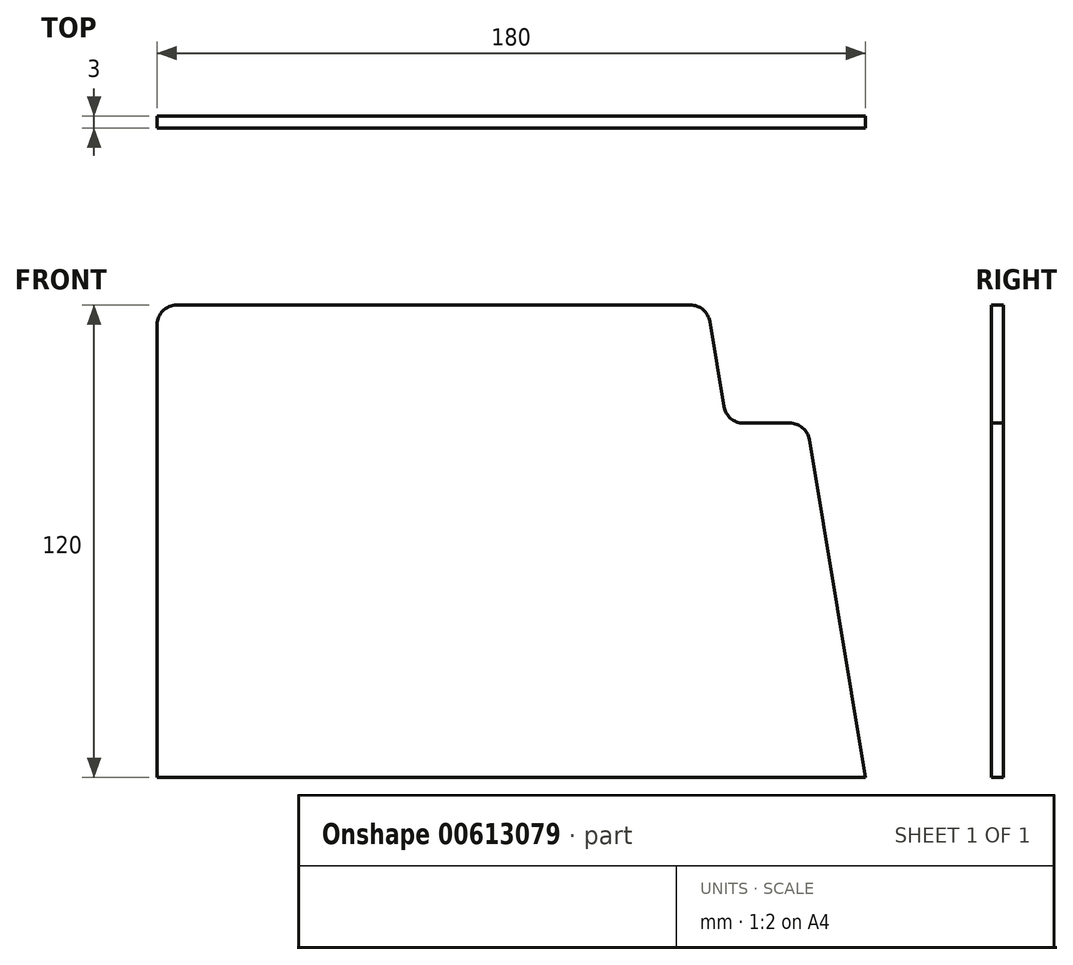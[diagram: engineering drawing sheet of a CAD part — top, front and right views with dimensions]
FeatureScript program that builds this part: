
annotation { "Feature Type Name" : "Feature", "Feature Type Description" : "" }
export const myFeature = defineFeature(function(context is Context, id is Id, definition is map)
    precondition{}
    {
        {
            var Q0;
            Q0=qCreatedBy(makeId("Front.planeOp"),FACE);
            var sketch = newSketch(context, id + "F0", { "sketchPlane" : qUnion([Q0])});
            skLineSegment(sketch, "E0.bottom", {"start": v(0, 0) * mm, "end": v(180, 0) * mm});
            skLineSegment(sketch, "E0.top", {"start": v(0, 120) * mm, "end": v(180, 120) * mm});
            skLineSegment(sketch, "E0.left", {"start": v(0, 0) * mm, "end": v(0, 120) * mm});
            skLineSegment(sketch, "E0.right", {"start": v(180, 0) * mm, "end": v(180, 120) * mm});
            skLineSegment(sketch, "E1", {"start": v(180, 0) * mm, "end": v(160, 120) * mm});
            skLineSegment(sketch, "E2", {"start": v(0, 90) * mm, "end": v(165, 90) * mm});
            skLineSegment(sketch, "E3", {"start": v(0, 66.36) * mm, "end": v(168.94, 66.36) * mm});
            skLineSegment(sketch, "E4", {"start": v(144.72, 90) * mm, "end": v(139.72, 120) * mm});
            skSolve(sketch);
        }
        {
            var Q0;
            {var subQ3=sQuery(id+"F0.wireOp",EDGE,"E4");Q0=makeQuery(id+"F0.imprint","IMPRINT",FACE,{"disambiguationData":[TD([[makeQuery(id+"F0.imprint","IMPRINT",EDGE,{"derivedFrom":subQ3}),1.0]])]});}
            var Q1;
            {var subQ6=sQuery(id+"F0.wireOp",EDGE,"E3");Q1=makeQuery(id+"F0.imprint","IMPRINT",FACE,{"disambiguationData":[TD([[makeQuery(id+"F0.imprint","IMPRINT",EDGE,{"derivedFrom":subQ6}),1.0]])]});}
            var Q2;
            {var subQ0=sQuery(id+"F0.wireOp",EDGE,"E0.bottom");Q2=makeQuery(id+"F0.imprint","IMPRINT",FACE,{"disambiguationData":[TD([[makeQuery(id+"F0.imprint","IMPRINT",EDGE,{"derivedFrom":subQ0}),1.0]])]});}
            extrude(context, id + "F1", {"entities" : qUnion([Q0, Q1, Q2]), "depth" : 3 * mm, "offsetDistance" : 25.4 * mm});
        }
        {
            var Q0;
            Q0=makeQuery(id+"F1.opExtrude","SWEPT_EDGE",EDGE,{"disambiguationData":[OSD([sQuery(id+"F0.wireOp",EDGE,"E1"),sQuery(id+"F0.wireOp",EDGE,"E2")])]});
            var Q1;
            Q1=makeQuery(id+"F1.opExtrude","SWEPT_EDGE",EDGE,{"disambiguationData":[OSD([sQuery(id+"F0.wireOp",EDGE,"E2"),sQuery(id+"F0.wireOp",EDGE,"E4")])]});
            var Q2;
            Q2=makeQuery(id+"F1.opExtrude","SWEPT_EDGE",EDGE,{"disambiguationData":[OSD([sQuery(id+"F0.wireOp",EDGE,"E0.top"),sQuery(id+"F0.wireOp",EDGE,"E4")])]});
            var Q3;
            Q3=makeQuery(id+"F1.opExtrude","SWEPT_EDGE",EDGE,{"disambiguationData":[OSD([sQuery(id+"F0.wireOp",EDGE,"E0.top"),sQuery(id+"F0.wireOp",EDGE,"E0.left")])]});
            fillet(context, id + "F2", {"entities" : qUnion([Q0, Q1, Q2, Q3]), "radius" : 5 * mm, "tangentPropagation" : true, "allowEdgeOverflow" : false});
        }
    });
